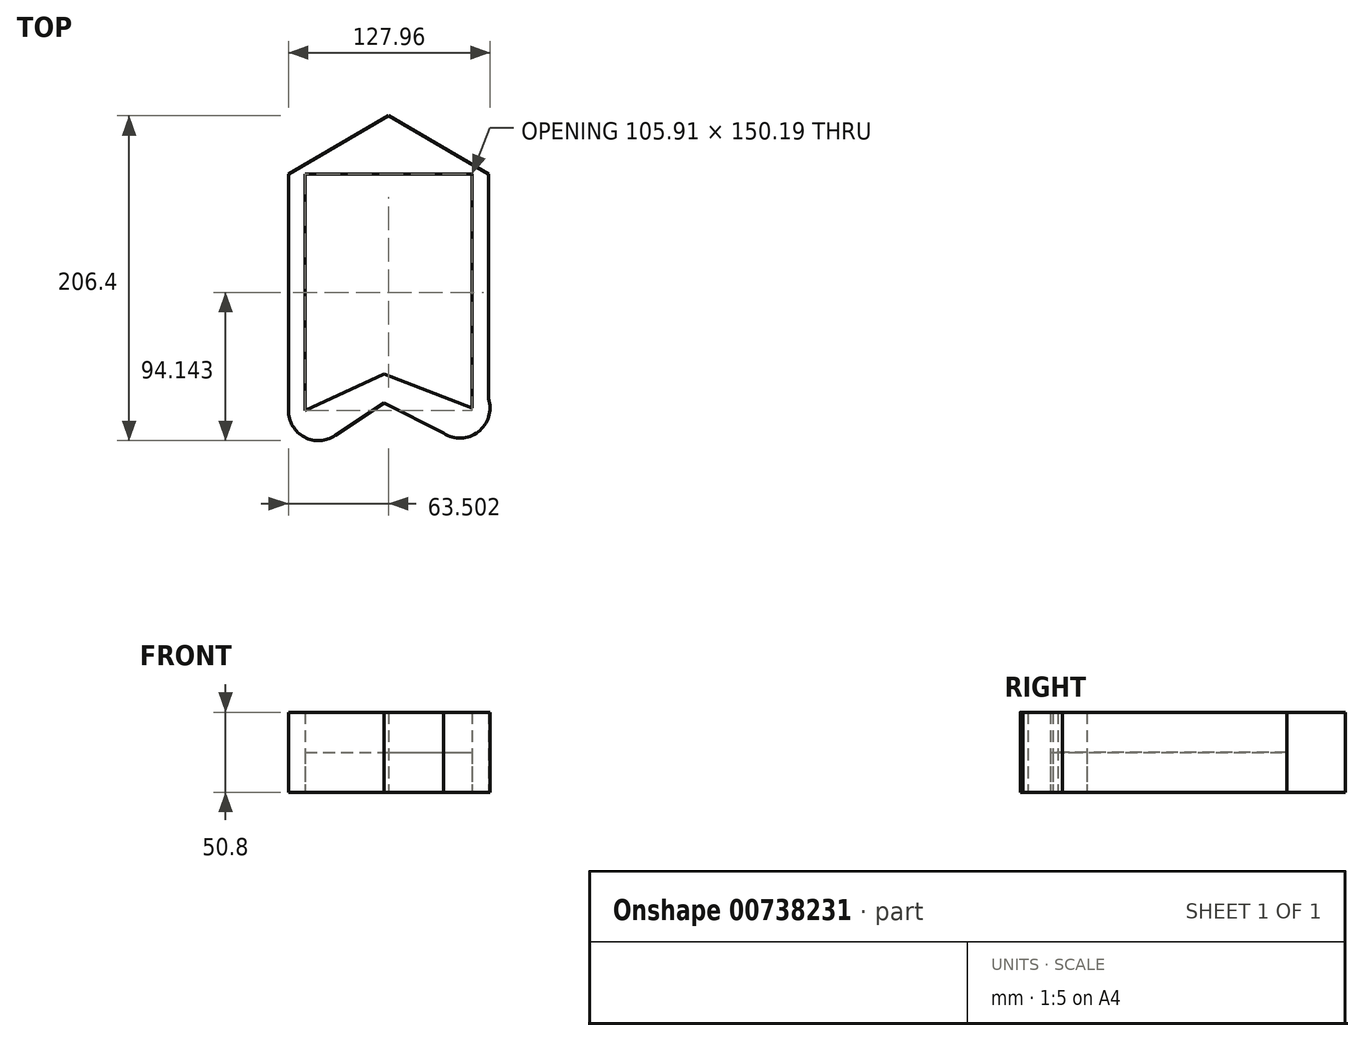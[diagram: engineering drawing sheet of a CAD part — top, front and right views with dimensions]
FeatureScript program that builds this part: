
annotation { "Feature Type Name" : "Feature", "Feature Type Description" : "" }
export const myFeature = defineFeature(function(context is Context, id is Id, definition is map)
    precondition{}
    {
        {
            var Q0;
            Q0=qCreatedBy(makeId("Top.planeOp"),FACE);
            var sketch = newSketch(context, id + "F0", { "sketchPlane" : qUnion([Q0])});
            skLineSegment(sketch, "E0", {"start": v(-77.9, 0) * mm, "end": v(-77.9, -150.2) * mm});
            skLineSegment(sketch, "E1", {"start": v(49.1, -147.91) * mm, "end": v(49.1, 0) * mm});
            skLineSegment(sketch, "E2", {"start": v(-48.27, -166.04) * mm, "end": v(-17.25, -145.36) * mm});
            skLineSegment(sketch, "E3", {"start": v(-17.25, -145.36) * mm, "end": v(21.47, -164.92) * mm});
            skLineSegment(sketch, "E4", {"start": v(-77.9, 0) * mm, "end": v(-14.4, 37.16) * mm});
            skLineSegment(sketch, "E5", {"start": v(-14.4, 37.16) * mm, "end": v(49.1, 0) * mm});
            skPoint(sketch, "E6.orphan", {"position": v(49.1, 37.16) * mm});
            skPoint(sketch, "E7.orphan", {"position": v(-77.9, 37.16) * mm});
            skArc(sketch, "E8.filletArc", {"start": v(-77.9, -150.2) * mm, "mid": v(-67.83, -167) * mm, "end": v(-48.27, -166.04) * mm});
            skArc(sketch, "E9.filletArc", {"start": v(49.1, -148.11) * mm, "mid": v(49.1, -148.01) * mm, "end": v(49.1, -147.91) * mm});
            skPoint(sketch, "E10.end.orphan", {"position": v(-58.84, -127.06) * mm});
            skPoint(sketch, "E11.start.orphan", {"position": v(18.62, -127.06) * mm});
            skArc(sketch, "E12.filletArc", {"start": v(20.59, -164.47) * mm, "mid": v(42.62, -163.64) * mm, "end": v(49.1, -142.57) * mm});
            skLineSegment(sketch, "E13", {"start": v(-77.9, 0) * mm, "end": v(49.1, 0) * mm});
            skLineSegment(sketch, "E14", {"start": v(-67.34, 0) * mm, "end": v(-67.34, -150.2) * mm});
            skLineSegment(sketch, "E15", {"start": v(-67.34, -150.2) * mm, "end": v(-17.25, -127.06) * mm});
            skLineSegment(sketch, "E16", {"start": v(-17.25, -127.06) * mm, "end": v(38.57, -148.53) * mm});
            skLineSegment(sketch, "E17", {"start": v(38.57, -148.53) * mm, "end": v(38.57, 0) * mm});
            skLineSegment(sketch, "E18", {"start": v(-29.24, 0) * mm, "end": v(-29.24, -132.6) * mm});
            skLineSegment(sketch, "E19", {"start": v(0.47, 0) * mm, "end": v(0.47, -133.87) * mm});
            skSolve(sketch);
        }
        {
            var Q0;
            {var subQ0=sQuery(id+"F0.wireOp",EDGE,"E14");Q0=makeQuery(id+"F0.imprint","IMPRINT",FACE,{"disambiguationData":[TD([[makeQuery(id+"F0.imprint","IMPRINT",EDGE,{"derivedFrom":subQ0}),1.0]])]});}
            var Q1;
            {var subQ0=sQuery(id+"F0.wireOp",EDGE,"E17");Q1=makeQuery(id+"F0.imprint","IMPRINT",FACE,{"disambiguationData":[TD([[makeQuery(id+"F0.imprint","IMPRINT",EDGE,{"derivedFrom":subQ0}),1.0]])]});}
            var Q2;
            {var subQ0=sQuery(id+"F0.wireOp",EDGE,"E18");Q2=makeQuery(id+"F0.imprint","IMPRINT",FACE,{"disambiguationData":[TD([[makeQuery(id+"F0.imprint","IMPRINT",EDGE,{"derivedFrom":subQ0}),1.0]])]});}
            extrude(context, id + "F1", {"entities" : qUnion([Q0, Q1, Q2]), "depth" : 25.4 * mm, "offsetDistance" : 25.4 * mm});
        }
        {
            var Q0;
            Q0 = qSketchRegion(id + "F0", true);
            extrude(context, id + "F2", {"entities" : qUnion([Q0]), "depth" : 50.8 * mm, "offsetDistance" : 25.4 * mm});
        }
    });
